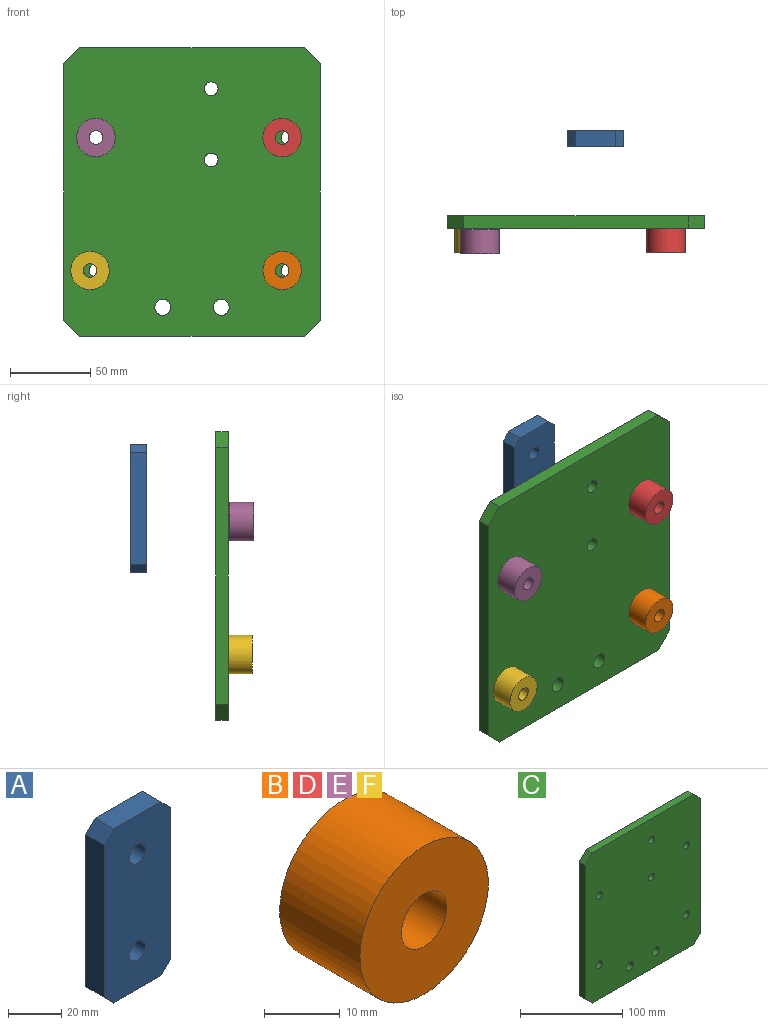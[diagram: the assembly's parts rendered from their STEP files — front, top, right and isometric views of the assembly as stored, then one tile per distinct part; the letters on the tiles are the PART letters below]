
ASSEMBLY  parts=6 mates=5
PART A: 12 faces, bbox 35x10x80 mm
  f0: plane 25x10mm, normal (0,0,1), area 250mm2, adj f6,f7,f10,f11
  f1: plane 70x10mm, normal (-1,0,0), area 700mm2, adj f6,f7,f9,f11
  f2: plane 25x10mm, normal (0,0,-1), area 250mm2, adj f6,f7,f8,f9
  f3: cylinder r=4.25mm len=10mm, axis (0,1,0), area 267mm2, adj f6,f7
  f4: cylinder r=4.25mm len=10mm, axis (0,1,0), area 267mm2, adj f6,f7
  f5: plane 70x10mm, normal (1,0,0), area 700mm2, adj f6,f7,f8,f10
  f6: plane 80x35mm, normal (0,-1,0), area 2636.5mm2, adj f0,f1,f2,f3,f4,f5,f8,f9
  f7: plane 80x35mm, normal (0,1,0), area 2636.5mm2, adj f0,f1,f2,f3,f4,f5,f8,f9
  f8: plane 10x5mm, normal (0.71,0,-0.71), area 70.7mm2, adj f2,f5,f6,f7
  f9: plane 10x5mm, normal (-0.71,0,-0.71), area 70.7mm2, adj f1,f2,f6,f7
  f10: plane 10x5mm, normal (0.71,0,0.71), area 70.7mm2, adj f0,f5,f6,f7
  f11: plane 10x5mm, normal (-0.71,0,0.71), area 70.7mm2, adj f0,f1,f6,f7
PART B: 4 faces, bbox 24x15x24 mm
  f0: cylinder r=4.25mm len=15mm, axis (0,1,0), area 400.6mm2, adj f2,f3
  f1: cylinder r=12mm len=24mm, axis (0,1,0), area 1131mm2, adj f2,f3
  f2: plane 24x24mm, normal (0,-1,0), area 395.6mm2, adj f0,f1
  f3: plane 24x24mm, normal (0,1,0), area 395.6mm2, adj f0,f1
PART C: 18 faces, bbox 160x8x180 mm
  f0: plane 140x8mm, normal (0,0,1), area 1120mm2, adj f12,f13,f16,f17
  f1: plane 160x8mm, normal (-1,0,0), area 1280mm2, adj f12,f13,f14,f17
  f2: plane 140x8mm, normal (0,0,-1), area 1120mm2, adj f12,f13,f14,f15
  f3: cylinder r=5mm len=10mm, axis (0,1,0), area 251.3mm2, adj f12,f13
  f4: cylinder r=5mm len=10mm, axis (0,1,0), area 251.3mm2, adj f12,f13
  f5: cylinder r=4.25mm len=8.5mm, axis (0,1,0), area 213.6mm2, adj f12,f13
  f6: cylinder r=4.25mm len=8.5mm, axis (0,1,0), area 213.6mm2, adj f12,f13
  f7: cylinder r=4.25mm len=8.5mm, axis (0,1,0), area 213.6mm2, adj f12,f13
  f8: cylinder r=4.25mm len=8.5mm, axis (0,1,0), area 213.6mm2, adj f12,f13
  f9: cylinder r=4.25mm len=8.5mm, axis (0,1,0), area 213.6mm2, adj f12,f13
  f10: cylinder r=4.25mm len=8.5mm, axis (0,1,0), area 213.6mm2, adj f12,f13
  f11: plane 160x8mm, normal (1,0,0), area 1280mm2, adj f12,f13,f15,f16
  f12: plane 180x160mm, normal (0,-1,0), area 28102.5mm2, adj f0,f1,f2,f3,f4,f5,f6,f7
  f13: plane 180x160mm, normal (0,1,0), area 28102.5mm2, adj f0,f1,f2,f3,f4,f5,f6,f7
  f14: plane 10x10mm, normal (-0.71,0,-0.71), area 113.1mm2, adj f1,f2,f12,f13
  f15: plane 10x10mm, normal (0.71,0,-0.71), area 113.1mm2, adj f2,f11,f12,f13
  f16: plane 10x10mm, normal (0.71,0,0.71), area 113.1mm2, adj f0,f11,f12,f13
  f17: plane 10x10mm, normal (-0.71,0,0.71), area 113.1mm2, adj f0,f1,f12,f13
PART D: same geometry as B
PART E: same geometry as B
PART F: same geometry as B
PLACE A rot(axis=(0,0,-1),180deg) t=(15.99,38.41,-89.61)mm
PLACE B rot(axis=(1,0,0),180deg) t=(60.3,-27.79,-180.86)mm
PLACE C t=(3.99,-4.79,-131.86)mm
PLACE D rot(axis=(0.45,0,-0.89),180deg) t=(60.3,-27.79,-97.86)mm
PLACE E t=(-56.01,-13.45,-97.86)mm
PLACE F rot(axis=(1,0,0),180deg) t=(-59.7,-27.79,-180.86)mm
MATE cylindrical A.f3 <-> C.f6  axis (0,-1,0) through (15.99,38.41,-67.36)mm
MATE pin_slot B.f0 <-> C.f8  axis (0,1,0) through (60.3,-12.79,-180.86)mm
MATE pin_slot D.f0 <-> C.f7  axis (0,1,0) through (60.3,-12.79,-97.86)mm
MATE cylindrical E.f0 <-> C.f10  axis (0,1,0) through (-56.01,-13.45,-97.86)mm
MATE pin_slot F.f0 <-> C.f9  axis (0,1,0) through (-59.7,-12.79,-180.86)mm
